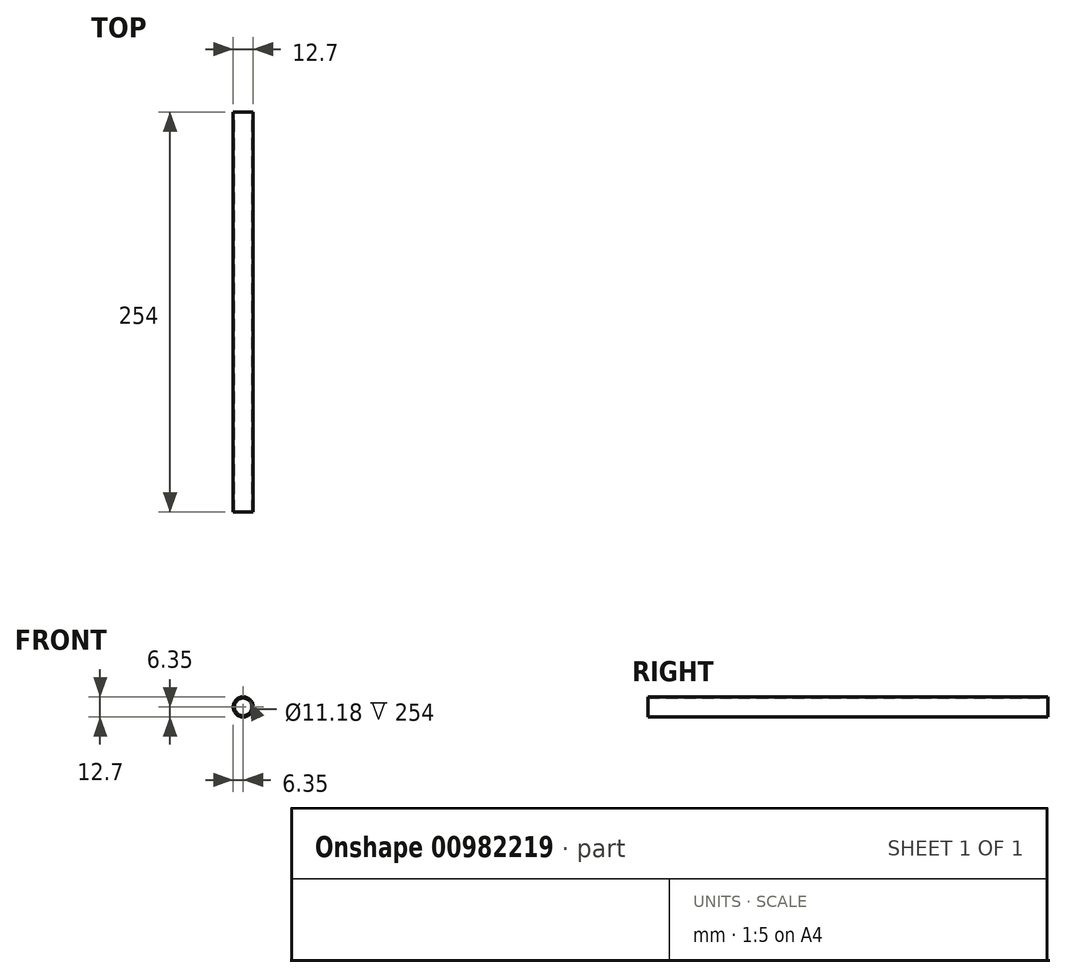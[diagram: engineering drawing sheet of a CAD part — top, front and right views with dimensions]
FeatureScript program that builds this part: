
annotation { "Feature Type Name" : "Feature", "Feature Type Description" : "" }
export const myFeature = defineFeature(function(context is Context, id is Id, definition is map)
    precondition{}
    {
        {
            var Q0;
            Q0=qCreatedBy(makeId("Front.planeOp"),FACE);
            var sketch = newSketch(context, id + "F0", { "sketchPlane" : qUnion([Q0])});
            skCircle(sketch, "E0", {"center": v(0, 0) * mm, "radius": 6.35 * mm});
            skSolve(sketch);
        }
        {
            var Q0;
            Q0=makeQuery(id+"F0.imprint","IMPRINT",FACE,{"disambiguationData":[TD([[makeQuery(id+"F0.imprint","IMPRINT",EDGE,{"derivedFrom":sQuery(id+"F0.wireOp",EDGE,"E0")}),1.0]])]});
            extrude(context, id + "F1", {"entities" : qUnion([Q0]), "oppositeDirection" : true, "depth" : 254 * mm, "offsetDistance" : 25.4 * mm});
        }
        {
            var Q0;
            Q0=makeQuery(id+"F1.opExtrude","CAP_FACE",FACE,{"disambiguationData":[OSD([sQuery(id+"F0.wireOp",EDGE,"E0")])],"isStart":false});
            var sketch = newSketch(context, id + "F2", { "sketchPlane" : qUnion([Q0])});
            skCircle(sketch, "E1", {"center": v(0, 0) * mm, "radius": 5.59 * mm});
            skSolve(sketch);
        }
        {
            var Q0;
            Q0=makeQuery(id+"F2.imprint","IMPRINT",FACE,{"disambiguationData":[TD([[makeQuery(id+"F2.imprint","IMPRINT",EDGE,{"derivedFrom":sQuery(id+"F2.wireOp",EDGE,"E1")}),1.0]])]});
            extrude(context, id + "F3", {"entities" : qUnion([Q0]), "operationType" : NewBodyOperationType.REMOVE, "oppositeDirection" : true, "depth" : 254 * mm, "offsetDistance" : 25.4 * mm});
        }
    });
